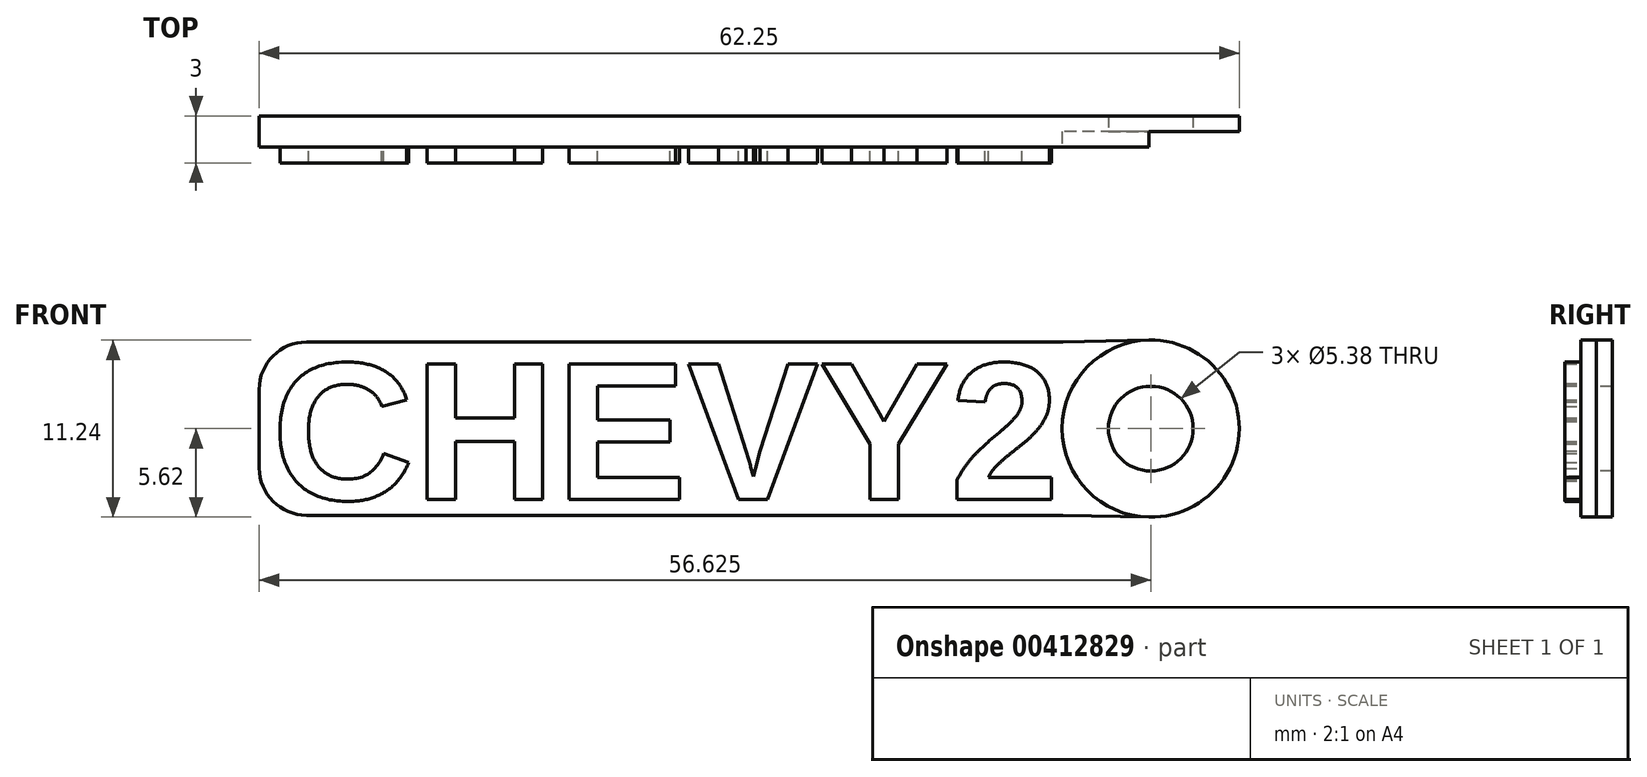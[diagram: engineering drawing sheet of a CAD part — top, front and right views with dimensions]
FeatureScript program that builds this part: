
annotation { "Feature Type Name" : "Feature", "Feature Type Description" : "" }
export const myFeature = defineFeature(function(context is Context, id is Id, definition is map)
    precondition{}
    {
        {
            var Q0;
            Q0=qCreatedBy(makeId("Front.planeOp"),FACE);
            var sketch = newSketch(context, id + "F0", { "sketchPlane" : qUnion([Q0])});
            skText(sketch, "E0", { "text": "CHEVY2", "fontName": "Arimo-Bold.ttf"});
            const initialGuessF0  = {"E0": [-0.0252, -0.009, 1, 0, 0.009]};
            skSetInitialGuess(sketch, initialGuessF0);
            skSolve(sketch);
        }
        {
            var Q0;
            Q0=qSketchRegion(id+"F0",true);
            extrude(context, id + "F1", {"entities" : qUnion([Q0]), "depth" : 1 * mm});
        }
        {
            var Q0;
            Q0=qCreatedBy(makeId("Front.planeOp"),FACE);
            var sketch = newSketch(context, id + "F2", { "sketchPlane" : qUnion([Q0])});
            skLineSegment(sketch, "E1", {"start": v(25, -10) * mm, "end": v(-26, -10) * mm});
            skLineSegment(sketch, "E2", {"start": v(-26, 1) * mm, "end": v(25, 1) * mm});
            skLineSegment(sketch, "E3", {"start": v(25, -10) * mm, "end": v(25, 1) * mm, "construction": true});
            skLineSegment(sketch, "E4", {"start": v(-26, -10) * mm, "end": v(-26, 1) * mm});
            skCircle(sketch, "E5", {"center": v(30.62, -4.5) * mm, "radius": 5.62 * mm});
            skLineSegment(sketch, "E6", {"start": v(25, -4.5) * mm, "end": v(67.35, -4.5) * mm, "construction": true});
            skPoint(sketch, "E6.endSnap0", {"position": v(25, -4.5) * mm});
            skLineSegment(sketch, "E7", {"start": v(25, 1) * mm, "end": v(30.5, 1.12) * mm});
            skLineSegment(sketch, "E8", {"start": v(30.5, -10.12) * mm, "end": v(25, -10) * mm});
            skCircle(sketch, "E9", {"center": v(30.62, -4.5) * mm, "radius": 2.69 * mm});
            skSolve(sketch);
        }
        {
            var Q0;
            Q0=qSketchRegion(id+"F2",true);
            extrude(context, id + "F3", {"entities" : qUnion([Q0]), "oppositeDirection" : true, "depth" : 2 * mm});
        }
        {
            var Q0;
            Q0=makeQuery(id+"F3.opExtrude","SWEPT_EDGE",EDGE,{"disambiguationData":[OSD([sQuery(id+"F2.wireOp",EDGE,"E2"),sQuery(id+"F2.wireOp",EDGE,"E4")])]});
            var Q1;
            Q1=makeQuery(id+"F3.opExtrude","SWEPT_EDGE",EDGE,{"disambiguationData":[OSD([sQuery(id+"F2.wireOp",EDGE,"E1"),sQuery(id+"F2.wireOp",EDGE,"E4")])]});
            var Q2;
            Q2=makeQuery(id+"F3.opExtrude","SWEPT_EDGE",EDGE,{"disambiguationData":[OSD([sQuery(id+"F2.wireOp",EDGE,"E1"),sQuery(id+"F2.wireOp",EDGE,"E8")])]});
            var Q3;
            Q3=makeQuery(id+"F3.opExtrude","SWEPT_EDGE",EDGE,{"disambiguationData":[OSD([sQuery(id+"F2.wireOp",EDGE,"E2"),sQuery(id+"F2.wireOp",EDGE,"E7")])]});
            fillet(context, id + "F4", {"entities" : qUnion([Q0, Q1, Q2, Q3]), "radius" : 3 * mm, "tangentPropagation" : true, "allowEdgeOverflow" : false});
        }
        {
            var Q0;
            Q0=makeQuery(id+"F3.opExtrude","CAP_FACE",FACE,{"disambiguationData":[OSD([sQuery(id+"F2.wireOp",EDGE,"E1"),sQuery(id+"F2.wireOp",EDGE,"E2"),sQuery(id+"F2.wireOp",EDGE,"E4"),sQuery(id+"F2.wireOp",EDGE,"E5"),sQuery(id+"F2.wireOp",EDGE,"E7"),sQuery(id+"F2.wireOp",EDGE,"E8"),sQuery(id+"F2.wireOp",EDGE,"E9")])],"isStart":true});
            var sketch = newSketch(context, id + "F5", { "sketchPlane" : qUnion([Q0])});
            skCircle(sketch, "E10", {"center": v(30.62, -4.5) * mm, "radius": 5.62 * mm});
            skSolve(sketch);
        }
        {
            var Q0;
            Q0=qSketchRegion(id+"F5",true);
            extrude(context, id + "F6", {"entities" : qUnion([Q0]), "operationType" : NewBodyOperationType.REMOVE, "oppositeDirection" : true, "depth" : 1 * mm});
        }
    });
